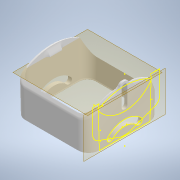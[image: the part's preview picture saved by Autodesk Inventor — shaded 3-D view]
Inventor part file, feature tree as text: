
AUTODESK INVENTOR PART (.ipt)
format: ipt  version: 2022 (Build 260153000, 153)  size: 889,344 bytes
history: native  units: mm
features: reference x18, sketch x16, projected_geometry x15, extrude x11, other x8, fillet x8, loft x2, mirror x2, chamfer x1
ambient origin geometry x8: Origin, YZ Plane, XZ Plane, XY Plane, X Axis, Y Axis, Z Axis, Center Point
bodies: Body1 (feature_tree)
feature tree (81):
  other  "Твердое тело1"
  sketch  "Эскиз1"
  other  "РабПлоскость1"
  loft  "Лофт1"
  other  "РабПлоскость3"
  sketch  "Эскиз8"
  sketch  "Эскиз9"
  sketch  "Эскиз10"
  extrude  "Выдавливание3"  Depth=0.3mm
  loft  "Лофт3"
  extrude  "Выдавливание4"  Depth=1.7mm
  extrude  "Выдавливание5"  TaperAngle=0.0deg  [1 undecoded]
  extrude  "Выдавливание6"  TaperAngle=0.0deg  [1 undecoded]
  extrude  "Выдавливание7"  Depth=50.0mm TaperAngle=0.0deg
  mirror  "Зеркальное отражение1"
  fillet  "Сопряжение6"  Radius=1.6mm
  fillet  "Сопряжение7"  Radius=1.6mm
  extrude  "Выдавливание8"  TaperAngle=0.0deg  [1 undecoded]
  mirror  "Зеркальное отражение2"
  extrude  "Выдавливание9"  TaperAngle=0.0deg  [1 undecoded]
  fillet  "Сопряжение8"  Radius=50.0mm
  fillet  "Сопряжение9"  Radius=50.0mm
  fillet  "Сопряжение10"  Radius=0.3mm
  extrude  "Выдавливание10"  Depth=7.0mm
  sketch  "Эскиз18"
  extrude  "Выдавливание11"  Depth=3.0mm
  extrude  "Выдавливание12"  Depth=1.5mm TaperAngle=0.0deg
  fillet  "Сопряжение12"  Radius=0.5mm
  fillet  "Сопряжение13"  Radius=1.0mm
  chamfer  "Фаска1"  Distance=2.0mm
  extrude  "Выдавливание13"  Depth=3.0mm
  fillet  "Сопряжение14"  Radius=0.006mm
  reference  "Ссылка1"
  reference  "Ссылка2"
  sketch  "Эскиз2"
  projected_geometry  "Спроецированная петля15"
  projected_geometry  "Спроецированная петля16"
  projected_geometry  "Спроецированная петля17"
  projected_geometry  "Спроецированная петля18"
  projected_geometry  "Спроецированная петля19"
  sketch  "Эскиз11"
  reference  "Ссылка7"
  reference  "Ссылка8"
  reference  "Ссылка9"
  sketch  "Эскиз12"
  projected_geometry  "Спроецированная петля20"
  sketch  "Эскиз13"
  projected_geometry  "Спроецированная петля21"
  sketch  "Эскиз14"
  projected_geometry  "Спроецированная петля22"
  sketch  "Эскиз15"
  projected_geometry  "Спроецированная петля23"
  sketch  "Эскиз16"
  projected_geometry  "Спроецированная петля24"
  reference  "Ссылка10"
  sketch  "Эскиз17"
  reference  "Ссылка11"
  reference  "Ссылка12"
  reference  "Ссылка13"
  reference  "Ссылка14"
  reference  "Ссылка15"
  projected_geometry  "Спроецированная петля25"
  sketch  "Эскиз19"
  reference  "Ссылка16"
  reference  "Ссылка17"
  reference  "Ссылка18"
  reference  "Ссылка19"
  projected_geometry  "Спроецированная петля26"
  sketch  "Эскиз20"
  projected_geometry  "Спроецированная петля27"
  reference  "Ссылка20"
  reference  "Ссылка21"
  reference  "Ссылка22"
  sketch  "Эскиз21"
  projected_geometry  "Спроецированная петля28"
  projected_geometry  "Спроецированная петля29"
  other  "<userpath>\Documents\Git\MZCAT_2024\MZCAT_4.iam"
  other  "MZCAT_4.iam"
  other  "LD19:1"
  other  "lidar_krestovina:1"
  other  "shatun_lidar:1"
note: 4 required parameter values undecoded (feature->parameter linkage not recoverable at this tier; creation-order binding heuristic only, values carry confidence <= 0.55)
